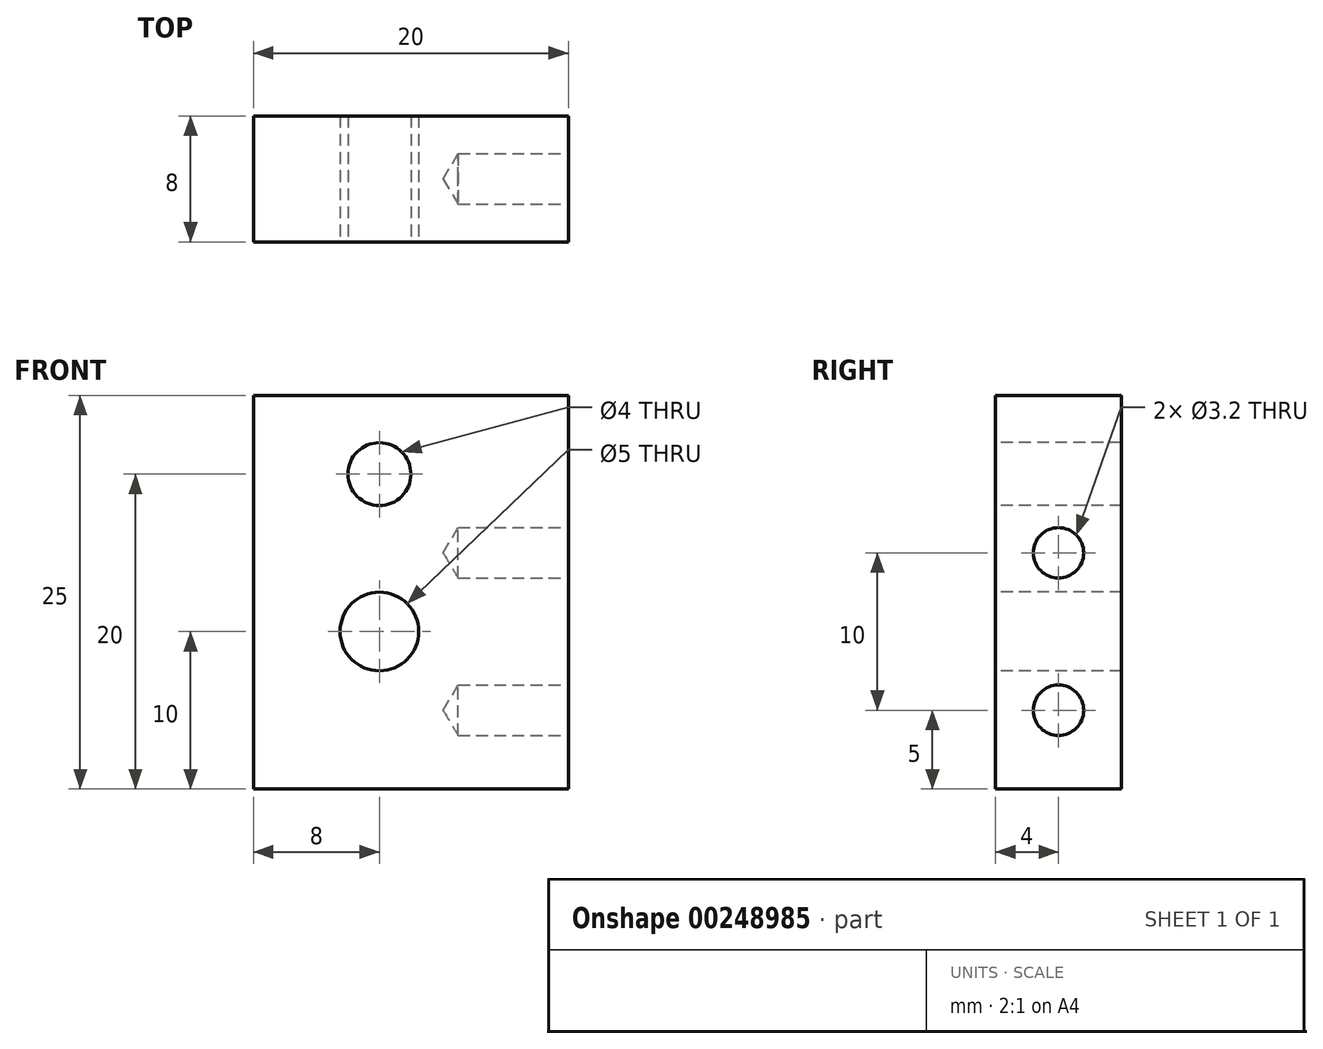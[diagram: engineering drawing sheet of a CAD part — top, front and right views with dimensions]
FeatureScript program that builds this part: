
annotation { "Feature Type Name" : "Feature", "Feature Type Description" : "" }
export const myFeature = defineFeature(function(context is Context, id is Id, definition is map)
    precondition{}
    {
        {
            var Q0;
            Q0=qCreatedBy(makeId("Front.planeOp"),FACE);
            var sketch = newSketch(context, id + "F0", { "sketchPlane" : qUnion([Q0])});
            skLineSegment(sketch, "E0.bottom", {"start": v(10, 12.5) * mm, "end": v(-10, 12.5) * mm});
            skLineSegment(sketch, "E0.top", {"start": v(10, -12.5) * mm, "end": v(-10, -12.5) * mm});
            skLineSegment(sketch, "E0.left", {"start": v(10, 12.5) * mm, "end": v(10, -12.5) * mm});
            skLineSegment(sketch, "E0.right", {"start": v(-10, 12.5) * mm, "end": v(-10, -12.5) * mm});
            skPoint(sketch, "E0.middle", {"position": v(0, 0) * mm});
            skSolve(sketch);
        }
        {
            var Q0;
            Q0=makeQuery(id+"F0.imprint","IMPRINT",FACE,{"disambiguationData":[TD([[makeQuery(id+"F0.imprint","IMPRINT",EDGE,{"derivedFrom":sQuery(id+"F0.wireOp",EDGE,"E0.bottom")}),1.0]])]});
            extrude(context, id + "F1", {"entities" : qUnion([Q0]), "endBound" : BoundingType.SYMMETRIC, "depth" : 8 * mm});
        }
        {
            var Q0;
            Q0=makeQuery(id+"F1.opExtrude","CAP_FACE",FACE,{"disambiguationData":[OSD([sQuery(id+"F0.wireOp",EDGE,"E0.bottom"),sQuery(id+"F0.wireOp",EDGE,"E0.top"),sQuery(id+"F0.wireOp",EDGE,"E0.left"),sQuery(id+"F0.wireOp",EDGE,"E0.right")])],"isStart":false});
            var sketch = newSketch(context, id + "F2", { "sketchPlane" : qUnion([Q0])});
            skPoint(sketch, "E1", {"position": v(-2, 7.5) * mm});
            skPoint(sketch, "E2", {"position": v(-2, -2.5) * mm});
            skSolve(sketch);
        }
        {
            var Q0;
            Q0=sQuery(id+"F2.wireOp",VERTEX,"E1");
            var Q1;
            Q1=makeQuery(id+"F1.opExtrude","SWEPT_BODY",BODY,{"disambiguationData":[OSD([sQuery(id+"F0.wireOp",EDGE,"E0.bottom"),sQuery(id+"F0.wireOp",EDGE,"E0.top"),sQuery(id+"F0.wireOp",EDGE,"E0.left"),sQuery(id+"F0.wireOp",EDGE,"E0.right")])]});
            hole(context, id + "F3", {"style" : HoleStyle.SIMPLE, "endStyle" : HoleEndStyle.THROUGH, "holeDiameter" : 4 * mm, "tappedDepth" : 4.2 * mm, "tapClearance" : 3, "startFromSketch" : true, "locations" : qUnion([Q0]), "scope" : qUnion([Q1])});
        }
        {
            var Q0;
            Q0=sQuery(id+"F2.wireOp",VERTEX,"E2");
            var Q1;
            Q1=makeQuery(id+"F1.opExtrude","SWEPT_BODY",BODY,{"disambiguationData":[OSD([sQuery(id+"F0.wireOp",EDGE,"E0.bottom"),sQuery(id+"F0.wireOp",EDGE,"E0.top"),sQuery(id+"F0.wireOp",EDGE,"E0.left"),sQuery(id+"F0.wireOp",EDGE,"E0.right")])]});
            hole(context, id + "F4", {"style" : HoleStyle.SIMPLE, "endStyle" : HoleEndStyle.THROUGH, "holeDiameter" : 5 * mm, "tappedDepth" : 4.2 * mm, "tapClearance" : 3, "startFromSketch" : true, "locations" : qUnion([Q0]), "scope" : qUnion([Q1])});
        }
        {
            var Q0;
            Q0=makeQuery(id+"F1.opExtrude","SWEPT_FACE",FACE,{"disambiguationData":[OSD([sQuery(id+"F0.wireOp",EDGE,"E0.left")])]});
            var sketch = newSketch(context, id + "F5", { "sketchPlane" : qUnion([Q0])});
            skPoint(sketch, "E3", {"position": v(0, 2.5) * mm});
            skPoint(sketch, "E4", {"position": v(0, -7.5) * mm});
            skSolve(sketch);
        }
        {
            var Q0;
            Q0=sQuery(id+"F5.wireOp",VERTEX,"E3");
            var Q1;
            Q1=sQuery(id+"F5.wireOp",VERTEX,"E4");
            var Q2;
            Q2=makeQuery(id+"F1.opExtrude","SWEPT_BODY",BODY,{"disambiguationData":[OSD([sQuery(id+"F0.wireOp",EDGE,"E0.bottom"),sQuery(id+"F0.wireOp",EDGE,"E0.top"),sQuery(id+"F0.wireOp",EDGE,"E0.left"),sQuery(id+"F0.wireOp",EDGE,"E0.right")])]});
            hole(context, id + "F6", {"style" : HoleStyle.SIMPLE, "endStyle" : HoleEndStyle.BLIND, "standardTappedOrClearance" : lookupTablePath({ "standard" : "ISO", "engagement" : "75%", "pitch" : "0.75 mm", "size" : "M4", "type" : "Tapped" }), "standardBlindInLast" : lookupTablePath({ "standard" : "ISO", "engagement" : "75%", "pitch" : "0.75 mm", "size" : "M4", "type" : "Tapped" }), "holeDiameter" : 3.2 * mm, "showTappedDepth" : true, "holeDepth" : 7 * mm, "tappedDepth" : 4.75 * mm, "tapClearance" : 3, "startFromSketch" : true, "locations" : qUnion([Q0, Q1]), "scope" : qUnion([Q2])});
        }
    });
